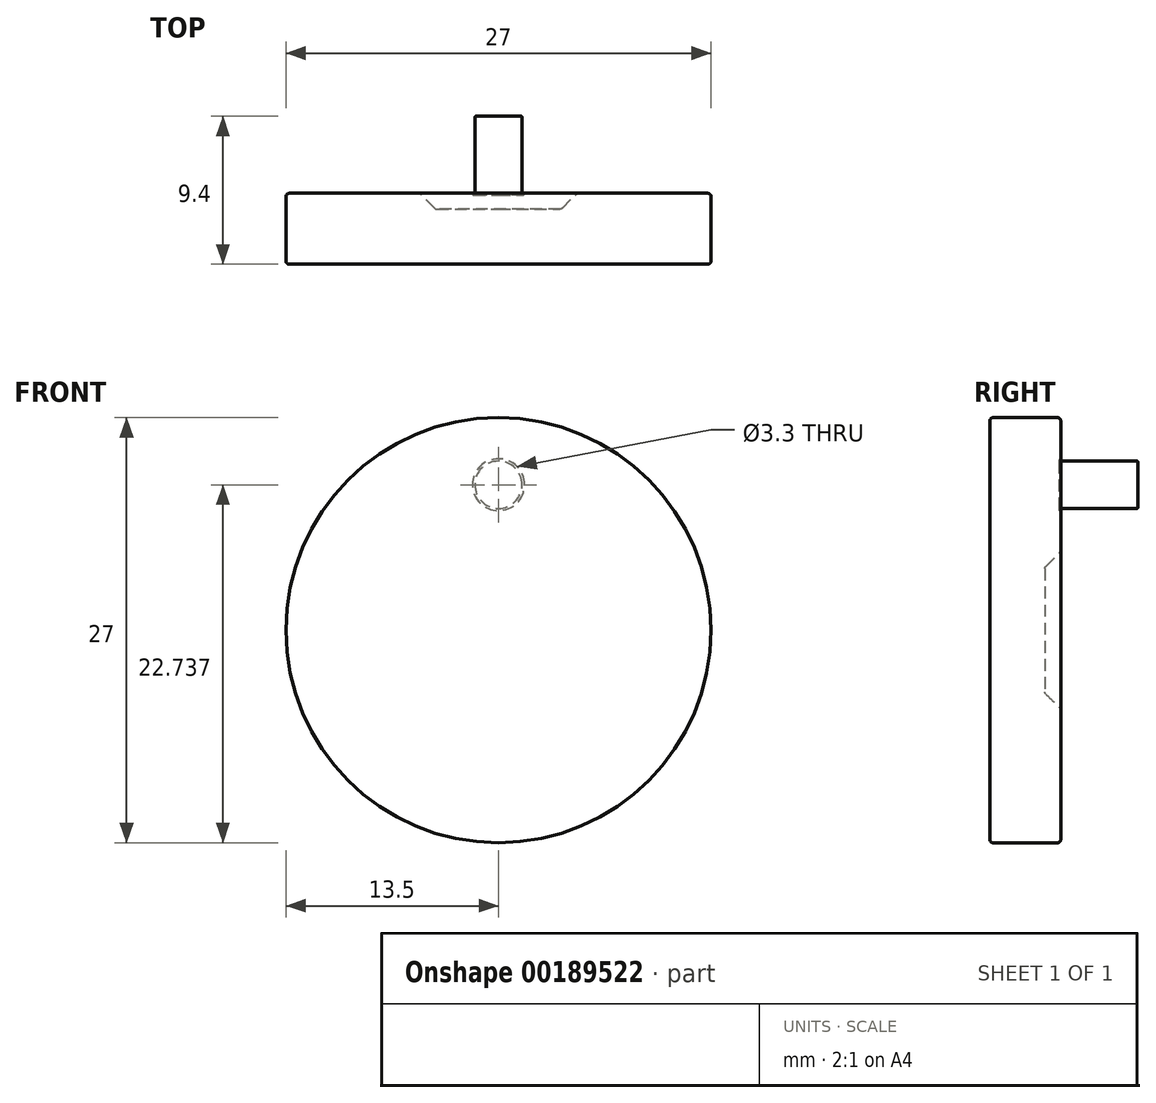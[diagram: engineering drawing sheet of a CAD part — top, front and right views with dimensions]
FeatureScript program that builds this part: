
annotation { "Feature Type Name" : "Feature", "Feature Type Description" : "" }
export const myFeature = defineFeature(function(context is Context, id is Id, definition is map)
    precondition{}
    {
        {
            var Q0;
            Q0=qCreatedBy(makeId("Front.planeOp"),FACE);
            var sketch = newSketch(context, id + "F0", { "sketchPlane" : qUnion([Q0])});
            skCircle(sketch, "E0", {"center": v(0, 0) * mm, "radius": 13.5 * mm});
            skSolve(sketch);
        }
        {
            var Q0;
            Q0=makeQuery(id+"F0.imprint","IMPRINT",FACE,{"disambiguationData":[TD([[makeQuery(id+"F0.imprint","IMPRINT",EDGE,{"derivedFrom":sQuery(id+"F0.wireOp",EDGE,"E0")}),1.0]])]});
            extrude(context, id + "F1", {"entities" : qUnion([Q0]), "depth" : 4.5 * mm});
        }
        {
            var Q0;
            Q0=qCreatedBy(makeId("Front.planeOp"),FACE);
            var sketch = newSketch(context, id + "F2", { "sketchPlane" : qUnion([Q0])});
            skCircle(sketch, "E1", {"center": v(0, 9.24) * mm, "radius": 1.5 * mm});
            skCircle(sketch, "E2", {"center": v(0, 9.24) * mm, "radius": 1.65 * mm});
            skSolve(sketch);
        }
        {
            var Q0;
            Q0=makeQuery(id+"F2.imprint","IMPRINT",FACE,{"disambiguationData":[TD([[makeQuery(id+"F2.imprint","IMPRINT",EDGE,{"derivedFrom":sQuery(id+"F2.wireOp",EDGE,"E1")}),1.0]])]});
            extrude(context, id + "F3", {"entities" : qUnion([Q0]), "operationType" : NewBodyOperationType.ADD, "oppositeDirection" : true, "depth" : 4.9 * mm});
        }
        {
            var Q0;
            Q0=makeQuery(id+"F2.imprint","IMPRINT",FACE,{"disambiguationData":[TD([[makeQuery(id+"F2.imprint","IMPRINT",EDGE,{"derivedFrom":sQuery(id+"F2.wireOp",EDGE,"E1")}),-1.0]])]});
            extrude(context, id + "F4", {"entities" : qUnion([Q0]), "operationType" : NewBodyOperationType.REMOVE, "depth" : 0.1 * mm});
        }
        {
            var Q0;
            Q0=makeQuery(id+"F4.boolean.opBoolean","COPY",FACE,{"derivedFrom":makeQuery(id+"F4.opExtrude","CAP_FACE",FACE,{"disambiguationData":[OSD([sQuery(id+"F2.wireOp",EDGE,"E1"),sQuery(id+"F2.wireOp",EDGE,"E2")])],"isStart":false})});
            var Q1;
            Q1=makeQuery(id+"F3.opExtrude","CAP_EDGE",EDGE,{"disambiguationData":[OSD([sQuery(id+"F2.wireOp",EDGE,"E1")])],"isStart":false});
            fillet(context, id + "F5", {"entities" : qUnion([Q0, Q1]), "radius" : 0.07 * mm, "tangentPropagation" : true, "allowEdgeOverflow" : false});
        }
        {
            var Q0;
            Q0=makeQuery(id+"F1.opExtrude","CAP_FACE",FACE,{"disambiguationData":[OSD([sQuery(id+"F0.wireOp",EDGE,"E0")])],"isStart":true});
            var sketch = newSketch(context, id + "F6", { "sketchPlane" : qUnion([Q0])});
            skCircle(sketch, "E3", {"center": v(0, 0) * mm, "radius": 5 * mm});
            skSolve(sketch);
        }
        {
            var Q0;
            Q0=makeQuery(id+"F6.imprint","IMPRINT",FACE,{"disambiguationData":[TD([[makeQuery(id+"F6.imprint","IMPRINT",EDGE,{"derivedFrom":sQuery(id+"F6.wireOp",EDGE,"E3")}),1.0]])]});
            extrude(context, id + "F7", {"entities" : qUnion([Q0]), "operationType" : NewBodyOperationType.REMOVE, "oppositeDirection" : true, "depth" : 1 * mm});
        }
        {
            var Q0;
            Q0=makeQuery(id+"F7.boolean.opBoolean","COPY",FACE,{"derivedFrom":makeQuery(id+"F7.opExtrude","CAP_FACE",FACE,{"disambiguationData":[OSD([sQuery(id+"F6.wireOp",EDGE,"E3")])],"isStart":false})});
            chamfer(context, id + "F8", {"entities" : qUnion([Q0]), "width" : 1 * mm, "tangentPropagation" : true});
        }
        {
            var Q0;
            Q0=makeQuery(id+"F1.opExtrude","CAP_EDGE",EDGE,{"disambiguationData":[OSD([sQuery(id+"F0.wireOp",EDGE,"E0")])],"isStart":true});
            var Q1;
            Q1=makeQuery(id+"F1.opExtrude","CAP_EDGE",EDGE,{"disambiguationData":[OSD([sQuery(id+"F0.wireOp",EDGE,"E0")])],"isStart":false});
            var Q2;
            Q2=makeQuery(id+"F8.opChamfer","BLEND_EDGE",EDGE,{"blendedFrom":[makeQuery(id+"F7.boolean.opBoolean","COPY",EDGE,{"derivedFrom":makeQuery(id+"F7.opExtrude","CAP_EDGE",EDGE,{"disambiguationData":[OSD([sQuery(id+"F6.wireOp",EDGE,"E3")])],"isStart":false})}),makeQuery(id+"F1.opExtrude","CAP_FACE",FACE,{"disambiguationData":[OSD([sQuery(id+"F0.wireOp",EDGE,"E0")])],"isStart":true})],"blendedInto":[makeQuery(id+"F1.opExtrude","CAP_FACE",FACE,{"disambiguationData":[OSD([sQuery(id+"F0.wireOp",EDGE,"E0")])],"isStart":true})]});
            var Q3;
            {var subQ0=sQuery(id+"F6.wireOp",EDGE,"E3");Q3=makeQuery(id+"F8.opChamfer","BLEND_EDGE",EDGE,{"blendedFrom":[makeQuery(id+"F7.boolean.opBoolean","COPY",EDGE,{"derivedFrom":makeQuery(id+"F7.opExtrude","CAP_EDGE",EDGE,{"disambiguationData":[OSD([subQ0])],"isStart":false})}),makeQuery(id+"F7.boolean.opBoolean","COPY",FACE,{"derivedFrom":makeQuery(id+"F7.opExtrude","CAP_FACE",FACE,{"disambiguationData":[OSD([subQ0])],"isStart":false})})],"blendedInto":[makeQuery(id+"F7.boolean.opBoolean","COPY",FACE,{"derivedFrom":makeQuery(id+"F7.opExtrude","CAP_FACE",FACE,{"disambiguationData":[OSD([subQ0])],"isStart":false})})]});}
            fillet(context, id + "F9", {"entities" : qUnion([Q0, Q1, Q2, Q3]), "radius" : 0.2 * mm, "tangentPropagation" : true, "allowEdgeOverflow" : false});
        }
    });
